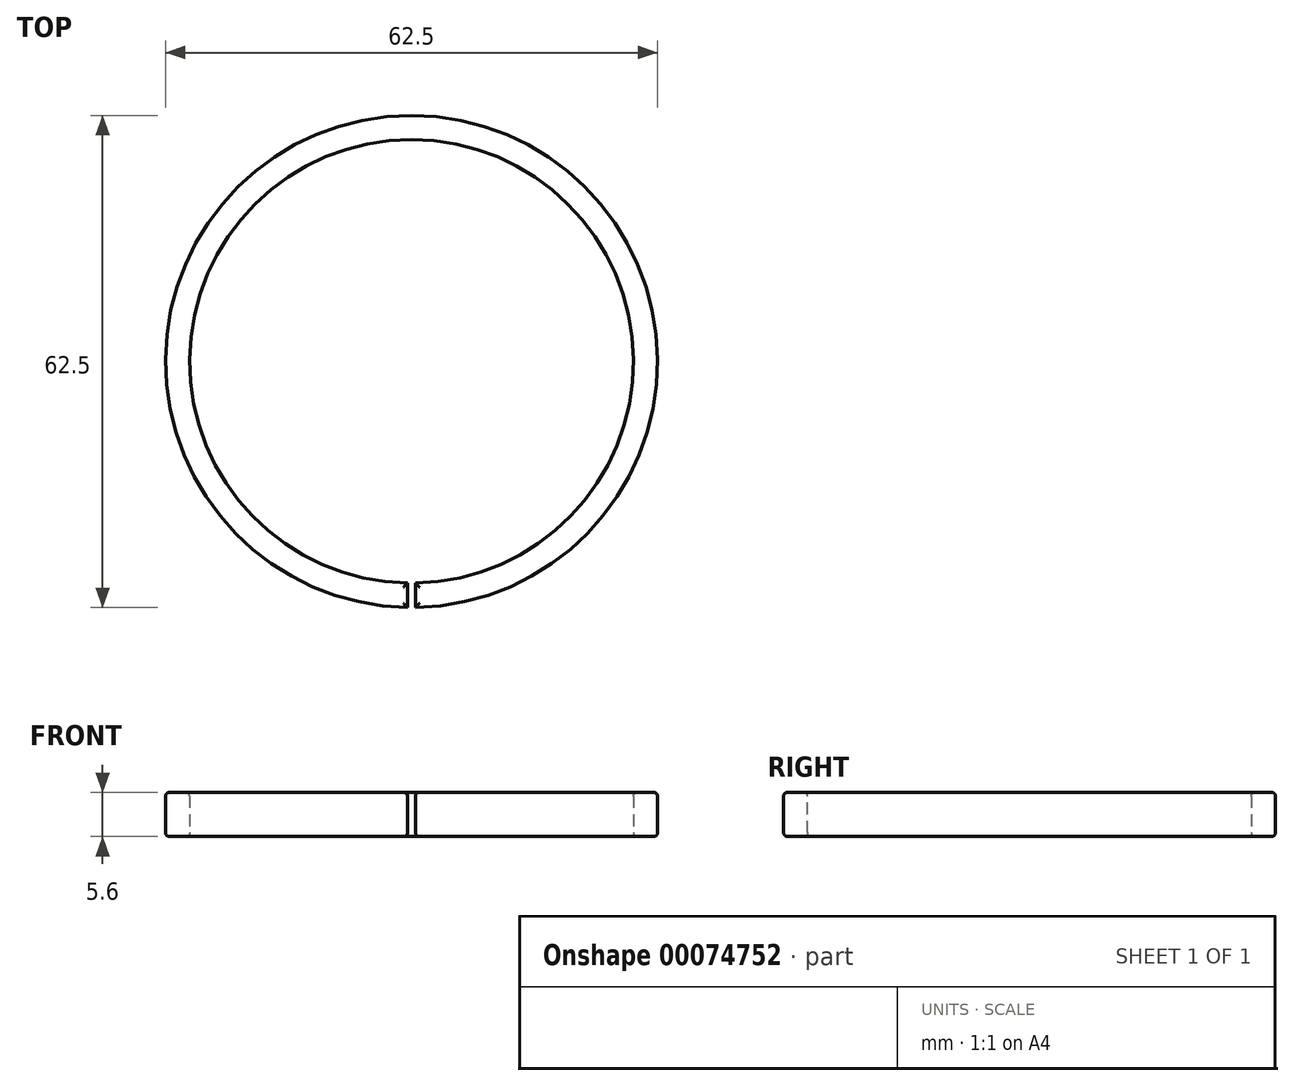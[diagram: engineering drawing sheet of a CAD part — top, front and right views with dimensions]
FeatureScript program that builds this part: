
annotation { "Feature Type Name" : "Feature", "Feature Type Description" : "" }
export const myFeature = defineFeature(function(context is Context, id is Id, definition is map)
    precondition{}
    {
        {
            var Q0;
            Q0=qCreatedBy(makeId("Top.planeOp"),FACE);
            var sketch = newSketch(context, id + "F0", { "sketchPlane" : qUnion([Q0])});
            skCircle(sketch, "E0.converted", {"center": v(0, 0) * mm, "radius": 28.18 * mm});
            skCircle(sketch, "E1.converted", {"center": v(0, 0) * mm, "radius": 31.25 * mm});
            skPoint(sketch, "E2.start.orphan", {"position": v(0, 31.25) * mm});
            skPoint(sketch, "E3.start.orphan", {"position": v(0, -31.25) * mm});
            skSolve(sketch);
        }
        {
            var Q0;
            Q0=makeQuery(id+"F0.imprint","IMPRINT",FACE,{"disambiguationData":[TD([[makeQuery(id+"F0.imprint","IMPRINT",EDGE,{"derivedFrom":sQuery(id+"F0.wireOp",EDGE,"E0.converted")}),-1.0]])]});
            extrude(context, id + "F1", {"entities" : qUnion([Q0]), "depth" : 5.6 * mm});
        }
        {
            var Q0;
            Q0=makeQuery(id+"F1.opExtrude","CAP_FACE",FACE,{"disambiguationData":[OSD([sQuery(id+"F0.wireOp",EDGE,"E0.converted"),sQuery(id+"F0.wireOp",EDGE,"E1.converted")])],"isStart":false});
            var sketch = newSketch(context, id + "F2", { "sketchPlane" : qUnion([Q0])});
            skLineSegment(sketch, "E4", {"start": v(0, -28.18) * mm, "end": v(0, -31.25) * mm, "construction": true});
            skLineSegment(sketch, "E5.0", {"start": v(-0.5, -28.18) * mm, "end": v(-0.5, -31.25) * mm});
            skLineSegment(sketch, "E6.0", {"start": v(0.5, -28.18) * mm, "end": v(0.5, -31.25) * mm});
            skArc(sketch, "E7.0", {"start": v(-0.5, -28.18) * mm, "mid": v(0, -28.18) * mm, "end": v(0.5, -28.18) * mm});
            skArc(sketch, "E8", {"start": v(-0.5, -31.25) * mm, "mid": v(0, -31.25) * mm, "end": v(0.5, -31.25) * mm});
            skSolve(sketch);
        }
        {
            var Q0;
            Q0=makeQuery(id+"F2.imprint","IMPRINT",FACE,{"disambiguationData":[TD([[makeQuery(id+"F2.imprint","IMPRINT",EDGE,{"derivedFrom":sQuery(id+"F2.wireOp",EDGE,"E5.0")}),1.0]])]});
            extrude(context, id + "F3", {"entities" : qUnion([Q0]), "operationType" : NewBodyOperationType.REMOVE, "oppositeDirection" : true, "depth" : 25 * mm});
        }
        {
            var Q0;
            Q0=makeQuery(id+"F3.boolean.opBoolean","COPY",EDGE,{"derivedFrom":makeQuery(id+"F3.opExtrude","SWEPT_EDGE",EDGE,{"disambiguationData":[OSD([sQuery(id+"F0.wireOp",EDGE,"E1.converted"),sQuery(id+"F2.wireOp",EDGE,"E5.0"),sQuery(id+"F2.wireOp",EDGE,"E8")])]})});
            var Q1;
            Q1=makeQuery(id+"F3.boolean.opBoolean","COPY",EDGE,{"derivedFrom":makeQuery(id+"F3.opExtrude","SWEPT_EDGE",EDGE,{"disambiguationData":[OSD([sQuery(id+"F0.wireOp",EDGE,"E0.converted"),sQuery(id+"F2.wireOp",EDGE,"E5.0"),sQuery(id+"F2.wireOp",EDGE,"E7.0")])]})});
            var Q2;
            Q2=makeQuery(id+"F3.boolean.opBoolean","COPY",EDGE,{"derivedFrom":makeQuery(id+"F3.opExtrude","SWEPT_EDGE",EDGE,{"disambiguationData":[OSD([sQuery(id+"F0.wireOp",EDGE,"E1.converted"),sQuery(id+"F2.wireOp",EDGE,"E6.0"),sQuery(id+"F2.wireOp",EDGE,"E8")])]})});
            var Q3;
            Q3=makeQuery(id+"F3.boolean.opBoolean","COPY",EDGE,{"derivedFrom":makeQuery(id+"F3.opExtrude","SWEPT_EDGE",EDGE,{"disambiguationData":[OSD([sQuery(id+"F0.wireOp",EDGE,"E0.converted"),sQuery(id+"F2.wireOp",EDGE,"E6.0"),sQuery(id+"F2.wireOp",EDGE,"E7.0")])]})});
            var Q4;
            Q4=makeQuery(id+"F1.opExtrude","CAP_FACE",FACE,{"disambiguationData":[OSD([sQuery(id+"F0.wireOp",EDGE,"E0.converted"),sQuery(id+"F0.wireOp",EDGE,"E1.converted")])],"isStart":false});
            var Q5;
            Q5=makeQuery(id+"F1.opExtrude","CAP_FACE",FACE,{"disambiguationData":[OSD([sQuery(id+"F0.wireOp",EDGE,"E0.converted"),sQuery(id+"F0.wireOp",EDGE,"E1.converted")])],"isStart":true});
            fillet(context, id + "F4", {"entities" : qUnion([Q0, Q1, Q2, Q3, Q4, Q5]), "radius" : .5 * mm, "tangentPropagation" : true, "allowEdgeOverflow" : false});
        }
    });
